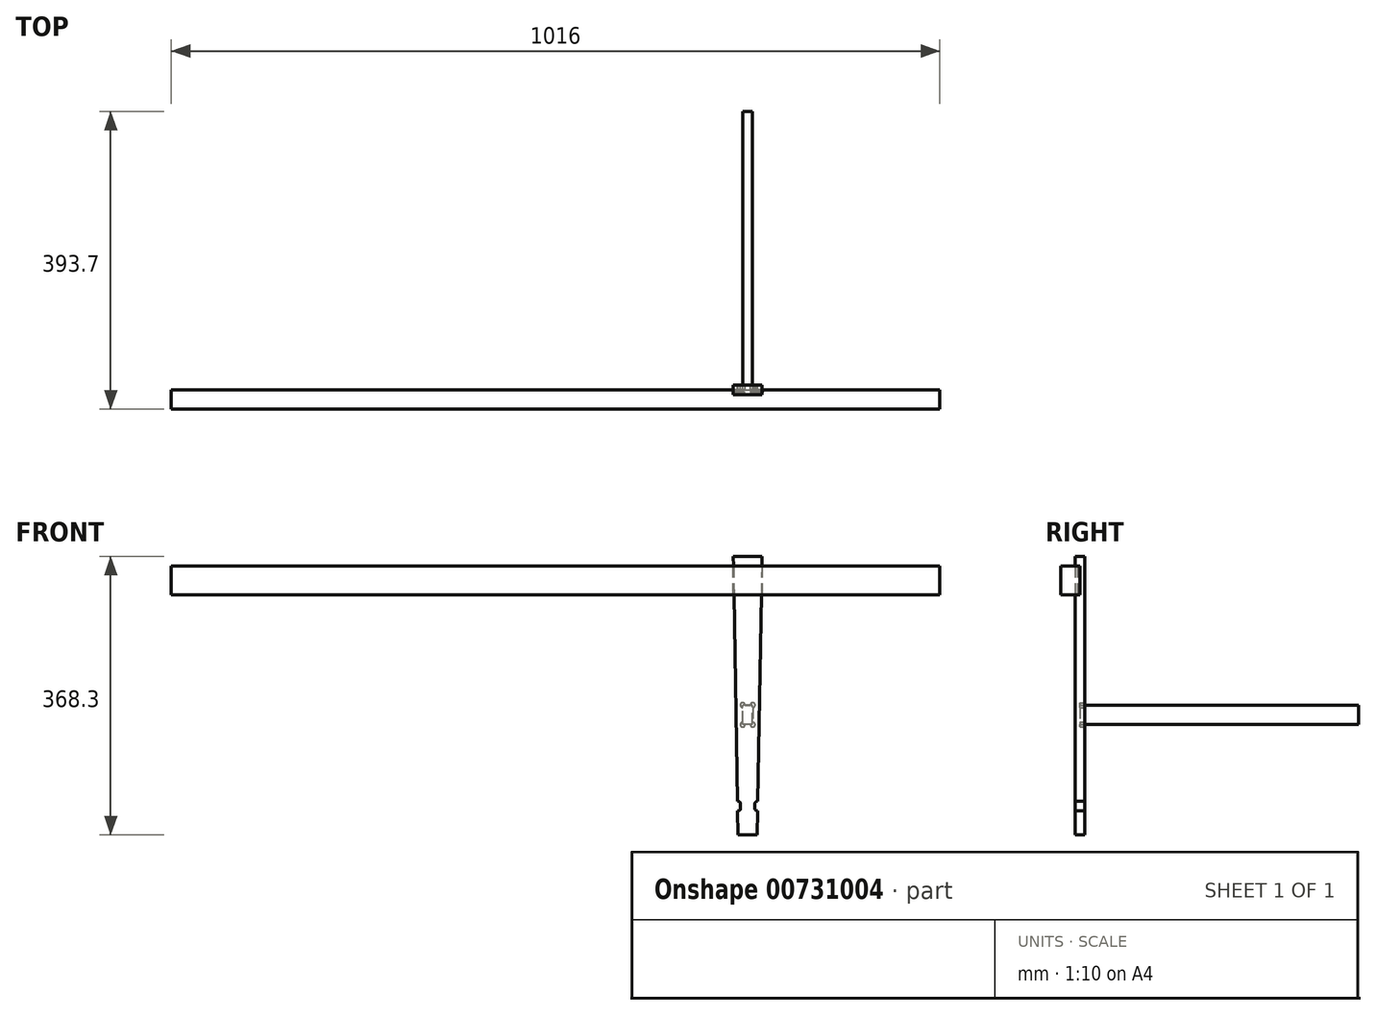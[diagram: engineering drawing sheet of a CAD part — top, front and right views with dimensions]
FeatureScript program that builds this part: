
annotation { "Feature Type Name" : "Feature", "Feature Type Description" : "" }
export const myFeature = defineFeature(function(context is Context, id is Id, definition is map)
    precondition{}
    {
        {
            var Q0;
            Q0=qCreatedBy(makeId("Front.planeOp"),FACE);
            var sketch = newSketch(context, id + "F0", { "sketchPlane" : qUnion([Q0])});
            skLineSegment(sketch, "E0.bottom", {"start": v(-19.05, 31.75) * mm, "end": v(19.05, 31.75) * mm});
            skLineSegment(sketch, "E0.top", {"start": v(-19.05, -336.55) * mm, "end": v(19.05, -336.55) * mm});
            skLineSegment(sketch, "E0.left", {"start": v(-19.05, 31.75) * mm, "end": v(-19.05, -336.55) * mm});
            skLineSegment(sketch, "E0.right", {"start": v(19.05, 31.75) * mm, "end": v(19.05, -336.55) * mm});
            skLineSegment(sketch, "E1", {"start": v(0, 31.75) * mm, "end": v(0, -336.55) * mm, "construction": true});
            skLineSegment(sketch, "E2.0", {"start": v(-12.7, 31.75) * mm, "end": v(-12.7, -336.55) * mm, "construction": true});
            skLineSegment(sketch, "E3.0", {"start": v(12.7, 31.75) * mm, "end": v(12.7, -336.55) * mm, "construction": true});
            skLineSegment(sketch, "E4", {"start": v(19.05, 31.75) * mm, "end": v(12.7, -336.55) * mm});
            skLineSegment(sketch, "E5", {"start": v(-19.05, 31.75) * mm, "end": v(-12.7, -336.55) * mm});
            skLineSegment(sketch, "E6", {"start": v(-34.35, -298.45) * mm, "end": v(34.98, -298.45) * mm, "construction": true});
            skLineSegment(sketch, "E7.bottom", {"start": v(12.7, -301.62) * mm, "end": v(-12.7, -301.62) * mm, "construction": true});
            skLineSegment(sketch, "E7.top", {"start": v(12.7, -295.28) * mm, "end": v(-12.7, -295.28) * mm, "construction": true});
            skLineSegment(sketch, "E7.left", {"start": v(12.7, -301.62) * mm, "end": v(12.7, -295.28) * mm, "construction": true});
            skLineSegment(sketch, "E7.right", {"start": v(-12.7, -301.62) * mm, "end": v(-12.7, -295.28) * mm, "construction": true});
            skPoint(sketch, "E7.middle", {"position": v(0, -298.45) * mm});
            skArc(sketch, "E8.0.startCap", {"start": v(15.87, -301.62) * mm, "mid": v(12.7, -304.8) * mm, "end": v(9.52, -301.62) * mm});
            skArc(sketch, "E8.0.endCap", {"start": v(9.52, -295.28) * mm, "mid": v(12.7, -292.1) * mm, "end": v(15.87, -295.28) * mm});
            skLineSegment(sketch, "E8.0.left", {"start": v(9.52, -301.62) * mm, "end": v(9.52, -295.28) * mm});
            skLineSegment(sketch, "E8.0.right", {"start": v(15.87, -301.62) * mm, "end": v(15.87, -295.28) * mm});
            skArc(sketch, "E9.0.startCap", {"start": v(-9.53, -301.62) * mm, "mid": v(-12.7, -304.8) * mm, "end": v(-15.88, -301.62) * mm});
            skArc(sketch, "E9.0.endCap", {"start": v(-15.88, -295.28) * mm, "mid": v(-12.7, -292.1) * mm, "end": v(-9.53, -295.28) * mm});
            skLineSegment(sketch, "E9.0.left", {"start": v(-15.88, -301.62) * mm, "end": v(-15.88, -295.28) * mm});
            skLineSegment(sketch, "E9.0.right", {"start": v(-9.53, -301.62) * mm, "end": v(-9.53, -295.28) * mm});
            skSolve(sketch);
        }
        {
            var Q0;
            Q0=makeQuery(id+"F0.imprint","IMPRINT",FACE,{"disambiguationData":[TD([[makeQuery(id+"F0.imprint","IMPRINT",EDGE,{"derivedFrom":sQuery(id+"F0.wireOp",EDGE,"E0.bottom")}),-1.0]])]});
            extrude(context, id + "F1", {"entities" : qUnion([Q0]), "endBound" : BoundingType.SYMMETRIC, "depth" : 12.7 * mm, "offsetDistance" : 25.4 * mm});
        }
        {
            var Q0;
            Q0=qCreatedBy(makeId("Front.planeOp"),FACE);
            var sketch = newSketch(context, id + "F2", { "sketchPlane" : qUnion([Q0])});
            skLineSegment(sketch, "E10.0.0", {"start": v(13.46, -292.2) * mm, "end": v(19.05, 31.75) * mm, "construction": true});
            skLineSegment(sketch, "E10.0.1", {"start": v(19.05, 31.75) * mm, "end": v(-19.05, 31.75) * mm, "construction": true});
            skLineSegment(sketch, "E10.0.2", {"start": v(-19.05, 31.75) * mm, "end": v(-13.46, -292.2) * mm, "construction": true});
            skLineSegment(sketch, "E10.0.3", {"start": v(-12.7, -336.55) * mm, "end": v(12.7, -336.55) * mm, "construction": true});
            skLineSegment(sketch, "E11.bottom", {"start": v(-762, 19.05) * mm, "end": v(254, 19.05) * mm});
            skLineSegment(sketch, "E11.top", {"start": v(-762, -19.05) * mm, "end": v(254, -19.05) * mm});
            skLineSegment(sketch, "E11.left", {"start": v(-762, 19.05) * mm, "end": v(-762, -19.05) * mm});
            skLineSegment(sketch, "E11.right", {"start": v(254, 19.05) * mm, "end": v(254, -19.05) * mm});
            skLineSegment(sketch, "E12", {"start": v(-762, 0) * mm, "end": v(254, 0) * mm, "construction": true});
            skPoint(sketch, "E13", {"position": v(0, 0) * mm});
            skSolve(sketch);
        }
        {
            var Q0;
            Q0=makeQuery(id+"F2.imprint","IMPRINT",FACE,{"disambiguationData":[TD([[makeQuery(id+"F2.imprint","IMPRINT",EDGE,{"derivedFrom":sQuery(id+"F2.wireOp",EDGE,"E11.bottom")}),-1.0]])]});
            extrude(context, id + "F3", {"entities" : qUnion([Q0]), "depth" : 25.4 * mm, "offsetDistance" : 25.4 * mm});
        }
        {
            var Q0;
            Q0=makeQuery(id+"F3.opExtrude","SWEPT_FACE",FACE,{"disambiguationData":[OSD([sQuery(id+"F2.wireOp",EDGE,"E11.bottom")])]});
            var sketch = newSketch(context, id + "F4", { "sketchPlane" : qUnion([Q0])});
            skLineSegment(sketch, "E14.0.0", {"start": v(19.05, 6.35) * mm, "end": v(-19.05, 6.35) * mm, "construction": true});
            skLineSegment(sketch, "E14.0.1", {"start": v(-19.05, 6.35) * mm, "end": v(-19.05, -6.35) * mm, "construction": true});
            skLineSegment(sketch, "E14.0.2", {"start": v(-19.05, -6.35) * mm, "end": v(19.05, -6.35) * mm, "construction": true});
            skLineSegment(sketch, "E14.0.3", {"start": v(19.05, -6.35) * mm, "end": v(19.05, 6.35) * mm, "construction": true});
            skLineSegment(sketch, "E15.0", {"start": v(-19.3, 6.6) * mm, "end": v(-19.3, -6.6) * mm, "construction": true});
            skLineSegment(sketch, "E15.1", {"start": v(19.3, 6.6) * mm, "end": v(-19.3, 6.6) * mm, "construction": true});
            skLineSegment(sketch, "E15.2", {"start": v(19.3, -6.6) * mm, "end": v(19.3, 6.6) * mm, "construction": true});
            skLineSegment(sketch, "E15.3", {"start": v(-19.3, -6.6) * mm, "end": v(19.3, -6.6) * mm, "construction": true});
            skLineSegment(sketch, "E16.bottom", {"start": v(-19.3, 0) * mm, "end": v(19.3, 0) * mm});
            skLineSegment(sketch, "E16.top", {"start": v(-19.3, -3.18) * mm, "end": v(19.3, -3.18) * mm});
            skLineSegment(sketch, "E16.left", {"start": v(-19.3, 0) * mm, "end": v(-19.3, -3.18) * mm});
            skLineSegment(sketch, "E16.right", {"start": v(19.3, 0) * mm, "end": v(19.3, -3.18) * mm});
            skLineSegment(sketch, "E17.0", {"start": v(-762, 0) * mm, "end": v(254, 0) * mm, "construction": true});
            skSolve(sketch);
        }
        {
            var Q0;
            Q0 = qSketchRegion(id + "F4", true);
            extrude(context, id + "F5", {"entities" : qUnion([Q0]), "operationType" : NewBodyOperationType.REMOVE, "endBound" : BoundingType.UP_TO_NEXT, "oppositeDirection" : true, "depth" : 25.4 * mm, "offsetDistance" : 25.4 * mm});
        }
        {
            var Q0;
            Q0=qCreatedBy(makeId("Right.planeOp"),FACE);
            var sketch = newSketch(context, id + "F6", { "sketchPlane" : qUnion([Q0])});
            skLineSegment(sketch, "E18.0.0", {"start": v(0, 19.05) * mm, "end": v(0, -19.05) * mm, "construction": true});
            skLineSegment(sketch, "E18.0.1", {"start": v(0, -19.05) * mm, "end": v(-25.4, -19.05) * mm, "construction": true});
            skLineSegment(sketch, "E18.0.2", {"start": v(-25.4, -19.05) * mm, "end": v(-25.4, 19.05) * mm, "construction": true});
            skLineSegment(sketch, "E18.0.3", {"start": v(-25.4, 19.05) * mm, "end": v(0, 19.05) * mm, "construction": true});
            skLineSegment(sketch, "E19.0", {"start": v(0.25, -19.3) * mm, "end": v(-25.65, -19.3) * mm, "construction": true});
            skLineSegment(sketch, "E19.1", {"start": v(0.25, 19.3) * mm, "end": v(0.25, -19.3) * mm, "construction": true});
            skLineSegment(sketch, "E19.2", {"start": v(-25.65, 19.3) * mm, "end": v(0.25, 19.3) * mm, "construction": true});
            skLineSegment(sketch, "E19.3", {"start": v(-25.65, -19.3) * mm, "end": v(-25.65, 19.3) * mm, "construction": true});
            skLineSegment(sketch, "E20.bottom", {"start": v(-3.18, 19.3) * mm, "end": v(-6.35, 19.3) * mm});
            skLineSegment(sketch, "E20.top", {"start": v(-3.17, -19.3) * mm, "end": v(-6.35, -19.3) * mm});
            skLineSegment(sketch, "E20.left", {"start": v(-3.18, 19.3) * mm, "end": v(-3.17, -19.3) * mm});
            skLineSegment(sketch, "E20.right", {"start": v(-6.35, 19.3) * mm, "end": v(-6.35, -19.3) * mm});
            skLineSegment(sketch, "E21.0", {"start": v(-6.35, 31.75) * mm, "end": v(-6.35, -292.2) * mm, "construction": true});
            skSolve(sketch);
        }
        {
            var Q0;
            Q0 = qSketchRegion(id + "F6", true);
            extrude(context, id + "F7", {"entities" : qUnion([Q0]), "operationType" : NewBodyOperationType.REMOVE, "endBound" : BoundingType.SYMMETRIC, "oppositeDirection" : true, "depth" : 38.1 * mm, "offsetDistance" : 25.4 * mm});
        }
        {
            var Q0;
            Q0=qCreatedBy(makeId("Front.planeOp"),FACE);
            var sketch = newSketch(context, id + "F8", { "sketchPlane" : qUnion([Q0])});
            skLineSegment(sketch, "E22", {"start": v(0, 0) * mm, "end": v(0, -210.52) * mm, "construction": true});
            skLineSegment(sketch, "E23", {"start": v(-96.43, -177.8) * mm, "end": v(102.25, -177.8) * mm, "construction": true});
            skLineSegment(sketch, "E24.bottom", {"start": v(6.35, -190.5) * mm, "end": v(-6.35, -190.5) * mm});
            skLineSegment(sketch, "E24.top", {"start": v(6.35, -165.1) * mm, "end": v(-6.35, -165.1) * mm});
            skLineSegment(sketch, "E24.left", {"start": v(6.35, -190.5) * mm, "end": v(6.35, -165.1) * mm});
            skLineSegment(sketch, "E24.right", {"start": v(-6.35, -190.5) * mm, "end": v(-6.35, -165.1) * mm});
            skPoint(sketch, "E24.middle", {"position": v(0, -177.8) * mm});
            skSolve(sketch);
        }
        {
            var Q0;
            Q0 = qSketchRegion(id + "F8", true);
            extrude(context, id + "F9", {"entities" : qUnion([Q0]), "oppositeDirection" : true, "depth" : 368.3 * mm, "offsetDistance" : 25.4 * mm});
        }
        {
            var Q0;
            Q0=makeQuery(id+"F1.opExtrude","CAP_FACE",FACE,{"disambiguationData":[OSD([sQuery(id+"F0.wireOp",EDGE,"E0.bottom"),sQuery(id+"F0.wireOp",EDGE,"E0.top"),sQuery(id+"F0.wireOp",EDGE,"E4"),sQuery(id+"F0.wireOp",EDGE,"E5")])],"isStart":true});
            var sketch = newSketch(context, id + "F10", { "sketchPlane" : qUnion([Q0])});
            skLineSegment(sketch, "E25.0.0", {"start": v(-6.35, -165.1) * mm, "end": v(-6.35, -190.5) * mm, "construction": true});
            skLineSegment(sketch, "E25.0.1", {"start": v(-6.35, -190.5) * mm, "end": v(6.35, -190.5) * mm, "construction": true});
            skLineSegment(sketch, "E25.0.2", {"start": v(6.35, -190.5) * mm, "end": v(6.35, -165.1) * mm, "construction": true});
            skLineSegment(sketch, "E25.0.3", {"start": v(6.35, -165.1) * mm, "end": v(-6.35, -165.1) * mm, "construction": true});
            skLineSegment(sketch, "E26.0", {"start": v(6.6, -164.85) * mm, "end": v(-6.6, -164.85) * mm});
            skLineSegment(sketch, "E26.1", {"start": v(6.6, -190.75) * mm, "end": v(6.6, -164.85) * mm});
            skLineSegment(sketch, "E26.2", {"start": v(-6.6, -190.75) * mm, "end": v(6.6, -190.75) * mm});
            skLineSegment(sketch, "E26.3", {"start": v(-6.6, -164.85) * mm, "end": v(-6.6, -190.75) * mm});
            skCircle(sketch, "E27", {"center": v(-6.6, -164.85) * mm, "radius": 3.17 * mm});
            skCircle(sketch, "E28", {"center": v(6.6, -164.85) * mm, "radius": 3.18 * mm});
            skCircle(sketch, "E29", {"center": v(6.6, -190.75) * mm, "radius": 3.18 * mm});
            skCircle(sketch, "E30", {"center": v(-6.6, -190.75) * mm, "radius": 3.18 * mm});
            skSolve(sketch);
        }
        {
            var Q0;
            Q0 = qSketchRegion(id + "F10", true);
            extrude(context, id + "F11", {"entities" : qUnion([Q0]), "operationType" : NewBodyOperationType.REMOVE, "oppositeDirection" : true, "depth" : 6.35 * mm, "offsetDistance" : 25.4 * mm});
        }
    });
